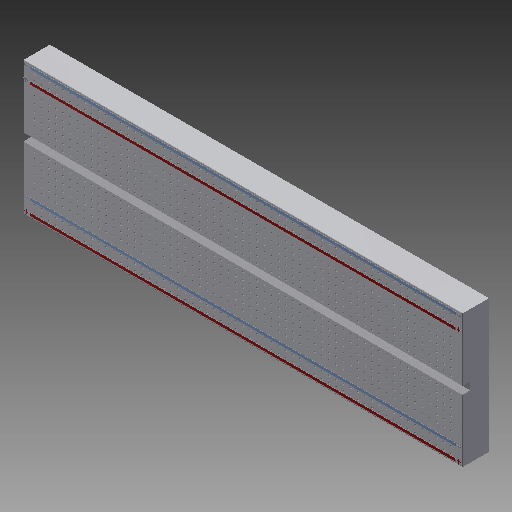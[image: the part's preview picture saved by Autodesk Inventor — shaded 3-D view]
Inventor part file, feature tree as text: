
AUTODESK INVENTOR PART (.ipt)
format: ipt  version: 2019 (Build 230136000, 136)  size: 1,122,304 bytes
history: native  units: mm
features: sketch x5, extrude x4, pattern_circular x2, hole x1, pattern_linear x1, mirror x1, fillet x1
ambient origin geometry x8: Origin, YZ Plane, XZ Plane, XY Plane, X Axis, Y Axis, Z Axis, Center Point
bodies: Solid1 (feature_tree)
feature tree (15):
  extrude  "Extrusion1"  Depth=50.0mm
  extrude  "Extrusion2"  Depth=10.0mm
  extrude  "Extrusion3"  Depth=3.0mm TaperAngle=0.0deg
  pattern_circular  "Circular Pattern1"  Count=16  [1 undecoded]
  hole  "Hole1"  [1 undecoded]
  pattern_linear  "Rectangular Pattern1"  Count1=16 Spacing1=1.0mm
  mirror  "Mirror1"
  pattern_circular  "Circular Pattern2"  Count=2 Angle=360.0deg
  extrude  "Extrusion4"  Depth=2.5mm
  fillet  "Fillet1"  Radius=2.5mm
  sketch  "Sketch1"  dims[d0=165.0mm d1=50.0mm]
  sketch  "Sketch2"  dims[d2=10.0mm d3=0.0mm d4=190.0mm]
  sketch  "Sketch3"  dims[d5=3.0mm d6=3.0mm d7=0.0mm d8=160.0mm]
  sketch  "Sketch4"  dims[d9=1.0mm d10=0.1mm d11=0.0mm d12=160.0mm d13=1.0mm d14=5.0mm d15=20.0mm d16=360.0deg]
  sketch  "Sketch5"  dims[d18=2.5mm d19=2.5mm d20=2.5mm d21=2.5mm d22=2.5mm d26=2.5mm d27=0.7mm d28=6.0mm d29=4.0mm d30=2.0mm d31=90.0deg d32=5.0mm d33=20.594885mm d34=300.0mm d36=2.7mm d37=20.0mm d38=360.0deg d40=0.1mm d41=0.0mm d42=0.2mm]
note: 2 required parameter values undecoded (feature->parameter linkage not recoverable at this tier; creation-order binding heuristic only, values carry confidence <= 0.55)
